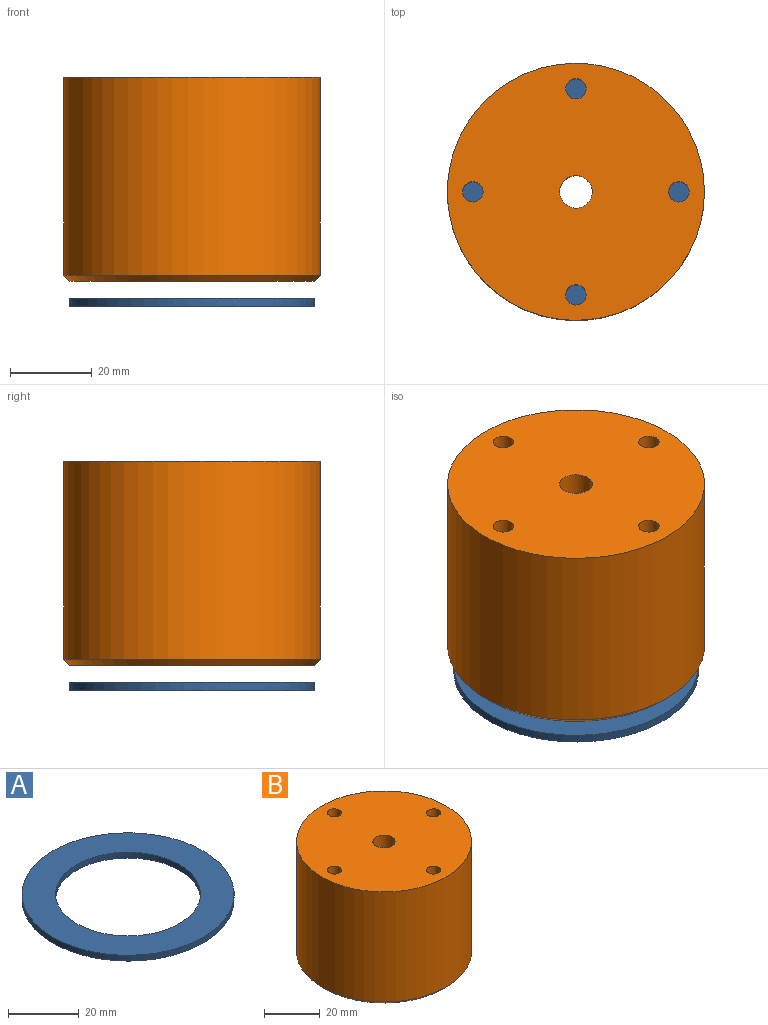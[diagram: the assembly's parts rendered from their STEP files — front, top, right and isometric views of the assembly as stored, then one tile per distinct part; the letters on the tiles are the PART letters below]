
ASSEMBLY  parts=2 mates=1
PART A: 4 faces, bbox 60x60x2 mm
  f0: cylinder r=20.5mm len=41mm, axis (0,0,-1), area 257.6mm2, adj f2,f3
  f1: cylinder r=30mm len=60mm, axis (0,0,-1), area 377mm2, adj f2,f3
  f2: plane 60x60mm, normal (0,0,1), area 1507.2mm2, adj f0,f1
  f3: plane 60x60mm, normal (0,0,-1), area 1507.2mm2, adj f0,f1
PART B: 14 faces, bbox 63x63x50 mm
  f0: cylinder r=2.5mm len=47mm, axis (0,0,-1), area 738.3mm2, adj f4,f7
  f1: cylinder r=2.5mm len=47mm, axis (0,0,-1), area 738.3mm2, adj f4,f7
  f2: cylinder r=2.5mm len=47mm, axis (0,0,-1), area 738.3mm2, adj f4,f7
  f3: cylinder r=31.5mm len=63mm, axis (0,0,-1), area 9599.1mm2, adj f4,f8
  f4: plane 63x63mm, normal (0,0,1), area 2988.4mm2, adj f0,f1,f2,f3,f12,f13
  f5: cylinder r=20.5mm len=41mm, axis (0,0,-1), area 386.4mm2, adj f7,f11
  f6: cylinder r=30mm len=60mm, axis (0,0,-1), area 565.5mm2, adj f7,f8
  f7: plane 60x60mm, normal (0,0,-1), area 1428.6mm2, adj f0,f1,f2,f5,f6,f13
  f8: cone r=31.5mm half-angle=45deg, axis (0,0,1), area 409.9mm2, adj f3,f6
  f9: cylinder r=19mm len=38mm, axis (0,0,-1), area 179.1mm2, adj f10,f11
  f10: plane 38x38mm, normal (0,0,-1), area 1083.8mm2, adj f9,f12
  f11: cone r=20.5mm half-angle=45deg, axis (0,0,-1), area 263.2mm2, adj f5,f9
  f12: cylinder r=4mm len=47mm, axis (0,0,-1), area 1181.2mm2, adj f4,f10
  f13: cylinder r=2.5mm len=47mm, axis (0,0,-1), area 738.3mm2, adj f4,f7
PLACE A t=(7.77,4.5,-0.72)mm
PLACE B t=(7.77,4.5,5.48)mm
MATE slider A.f0 <-> B.f5  axis (0,0,-1) through (7.77,4.5,-0.72)mm
